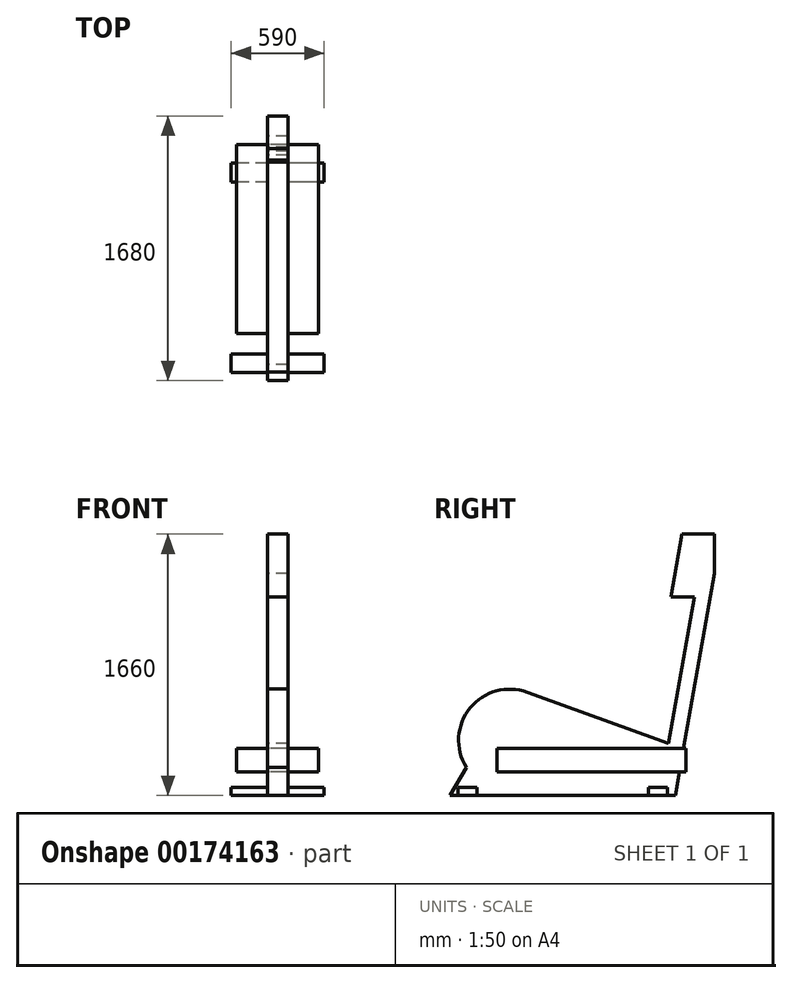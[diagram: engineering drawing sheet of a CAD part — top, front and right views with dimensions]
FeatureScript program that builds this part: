
annotation { "Feature Type Name" : "Feature", "Feature Type Description" : "" }
export const myFeature = defineFeature(function(context is Context, id is Id, definition is map)
    precondition{}
    {
        {
            var Q0;
            Q0=qCreatedBy(makeId("Right.planeOp"),FACE);
            var sketch = newSketch(context, id + "F0", { "sketchPlane" : qUnion([Q0])});
            skLineSegment(sketch, "E0", {"start": v(0, 0) * mm, "end": v(1431.38, 0) * mm});
            skLineSegment(sketch, "E1", {"start": v(1431.38, 0) * mm, "end": v(1680, 1410) * mm});
            skLineSegment(sketch, "E2", {"start": v(1680, 1410) * mm, "end": v(1680, 1660) * mm});
            skLineSegment(sketch, "E3", {"start": v(1680, 1660) * mm, "end": v(1472.54, 1660) * mm});
            skLineSegment(sketch, "E4", {"start": v(1472.54, 1660) * mm, "end": v(1402, 1260) * mm});
            skLineSegment(sketch, "E5", {"start": v(1402, 1260) * mm, "end": v(1552, 1260) * mm});
            skLineSegment(sketch, "E6", {"start": v(1552, 1260) * mm, "end": v(1387.85, 329.03) * mm});
            skLineSegment(sketch, "E7", {"start": v(1387.85, 329.03) * mm, "end": v(491.16, 655.4) * mm});
            skArc(sketch, "E8", {"start": v(491.16, 655.4) * mm, "mid": v(127.97, 555.2) * mm, "end": v(103.48, 179.23) * mm});
            skPoint(sketch, "E8.second.point", {"position": v(91.11, 201.1) * mm});
            skPoint(sketch, "E8.third.point", {"position": v(268.84, 655.4) * mm});
            skLineSegment(sketch, "E9", {"start": v(0, 0) * mm, "end": v(103.48, 179.23) * mm});
            skSolve(sketch);
        }
        {
            var Q0;
            Q0=makeQuery(id+"F0.imprint","IMPRINT",FACE,{"disambiguationData":[TD([[makeQuery(id+"F0.imprint","IMPRINT",EDGE,{"derivedFrom":sQuery(id+"F0.wireOp",EDGE,"E0")}),1.0]])]});
            extrude(context, id + "F1", {"entities" : qUnion([Q0]), "endBound" : BoundingType.SYMMETRIC, "depth" : 130 * mm});
        }
        {
            var Q0;
            Q0=qCreatedBy(makeId("Right.planeOp"),FACE);
            var sketch = newSketch(context, id + "F2", { "sketchPlane" : qUnion([Q0])});
            skLineSegment(sketch, "E10.bottom", {"start": v(300, 300) * mm, "end": v(1500, 300) * mm});
            skLineSegment(sketch, "E10.top", {"start": v(300, 150) * mm, "end": v(1500, 150) * mm});
            skLineSegment(sketch, "E10.left", {"start": v(300, 300) * mm, "end": v(300, 150) * mm});
            skLineSegment(sketch, "E10.right", {"start": v(1500, 300) * mm, "end": v(1500, 150) * mm});
            skSolve(sketch);
        }
        {
            var Q0;
            Q0=qSketchRegion(id+"F2",true);
            extrude(context, id + "F3", {"entities" : qUnion([Q0]), "operationType" : NewBodyOperationType.ADD, "endBound" : BoundingType.SYMMETRIC, "depth" : 520 * mm});
        }
        {
            var Q0;
            Q0=qCreatedBy(makeId("Right.planeOp"),FACE);
            var sketch = newSketch(context, id + "F4", { "sketchPlane" : qUnion([Q0])});
            skLineSegment(sketch, "E11.bottom", {"start": v(50, 0) * mm, "end": v(170, 0) * mm});
            skLineSegment(sketch, "E11.top", {"start": v(50, 50) * mm, "end": v(170, 50) * mm});
            skLineSegment(sketch, "E11.left", {"start": v(50, 0) * mm, "end": v(50, 50) * mm});
            skLineSegment(sketch, "E11.right", {"start": v(170, 0) * mm, "end": v(170, 50) * mm});
            skLineSegment(sketch, "E12", {"start": v(715.69, 0) * mm, "end": v(715.69, -232.94) * mm, "construction": true});
            skLineSegment(sketch, "E13.MirrorCS", {"start": v(1381.38, 50) * mm, "end": v(1261.38, 50) * mm});
            skLineSegment(sketch, "E14.MirrorCS", {"start": v(1381.38, 0) * mm, "end": v(1261.38, 0) * mm});
            skLineSegment(sketch, "E15.MirrorCS", {"start": v(1381.38, 0) * mm, "end": v(1381.38, 50) * mm});
            skLineSegment(sketch, "E16.MirrorCS", {"start": v(1261.38, 0) * mm, "end": v(1261.38, 50) * mm});
            skSolve(sketch);
        }
        {
            var Q0;
            Q0=qSketchRegion(id+"F4",true);
            extrude(context, id + "F5", {"entities" : qUnion([Q0]), "operationType" : NewBodyOperationType.ADD, "endBound" : BoundingType.SYMMETRIC, "depth" : 590 * mm});
        }
    });
